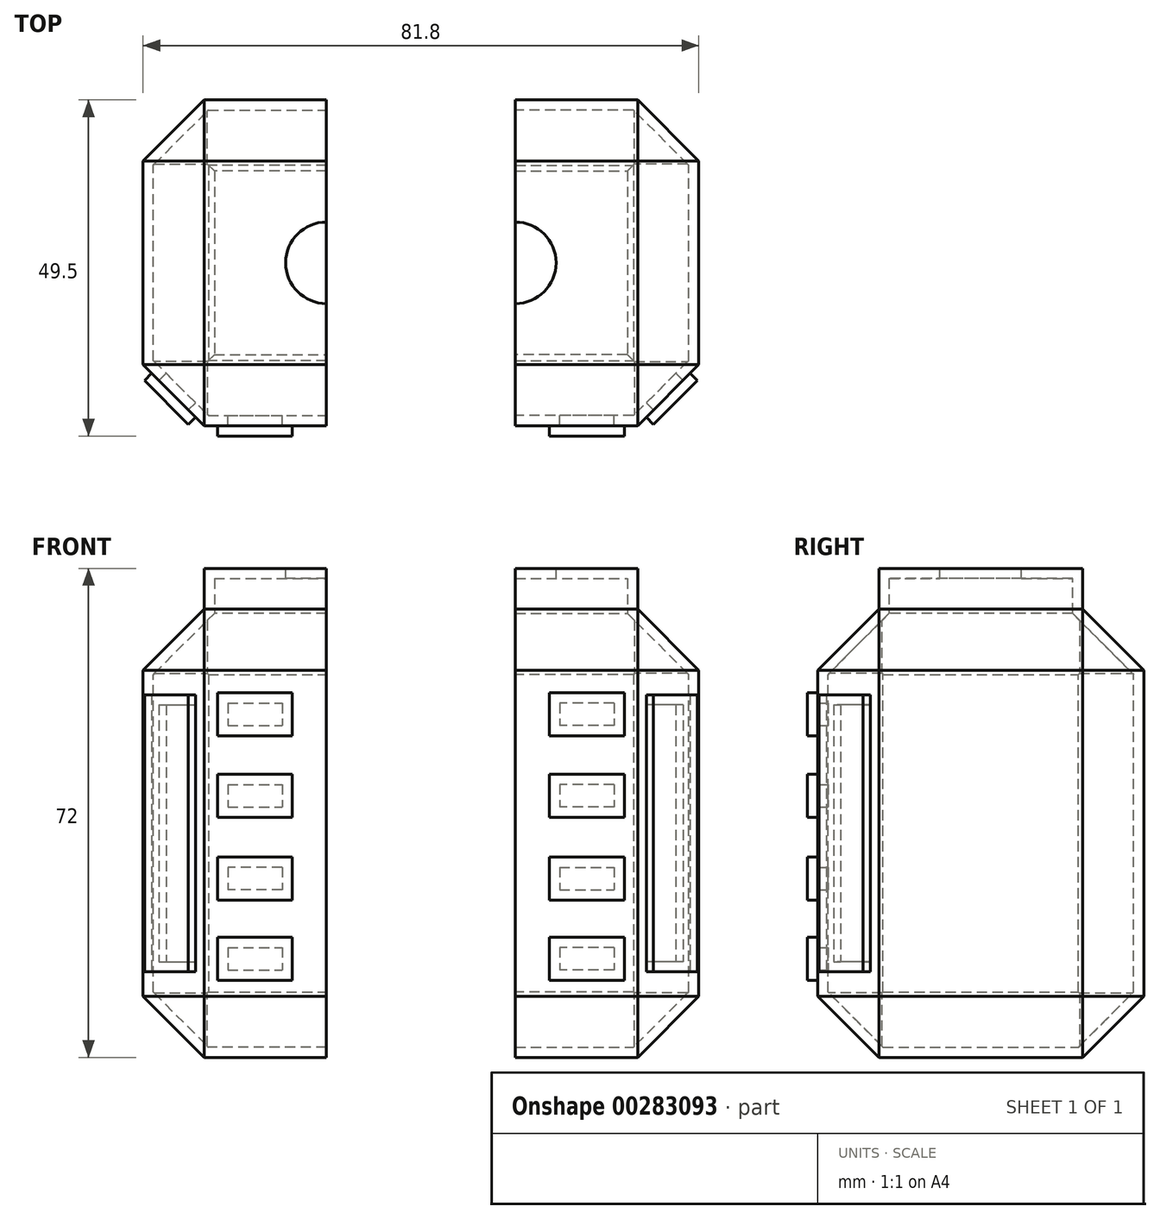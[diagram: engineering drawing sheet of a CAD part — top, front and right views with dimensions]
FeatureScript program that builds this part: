
annotation { "Feature Type Name" : "Feature", "Feature Type Description" : "" }
export const myFeature = defineFeature(function(context is Context, id is Id, definition is map)
    precondition{}
    {
        {
            var Q0;
            Q0=qCreatedBy(makeId("Front.planeOp"),FACE);
            var sketch = newSketch(context, id + "F0", { "sketchPlane" : qUnion([Q0])});
            skLineSegment(sketch, "E0.bottom", {"start": v(-51.64, 31.09) * mm, "end": v(38.36, 31.09) * mm});
            skLineSegment(sketch, "E0.top", {"start": v(-51.64, -78.91) * mm, "end": v(38.36, -78.91) * mm});
            skLineSegment(sketch, "E0.left", {"start": v(-51.64, 31.09) * mm, "end": v(-51.64, -78.91) * mm});
            skLineSegment(sketch, "E0.right", {"start": v(38.36, 31.09) * mm, "end": v(38.36, -78.91) * mm});
            skPoint(sketch, "E1.0", {"position": v(0, 0) * mm});
            skSolve(sketch);
        }
        {
            var Q0;
            Q0=makeQuery(id+"F0.imprint","IMPRINT",FACE,{"disambiguationData":[TD([[makeQuery(id+"F0.imprint","IMPRINT",EDGE,{"derivedFrom":sQuery(id+"F0.wireOp",EDGE,"E0.bottom")}),-1.0]])]});
            extrude(context, id + "F1", {"entities" : qUnion([Q0]), "depth" : 80 * mm});
        }
        {
            var Q0;
            Q0=makeQuery(id+"F1.opExtrude","CAP_EDGE",EDGE,{"disambiguationData":[OSD([sQuery(id+"F0.wireOp",EDGE,"E0.left")])],"isStart":true});
            var Q1;
            Q1=makeQuery(id+"F1.opExtrude","SWEPT_EDGE",EDGE,{"disambiguationData":[OSD([sQuery(id+"F0.wireOp",EDGE,"E0.bottom"),sQuery(id+"F0.wireOp",EDGE,"E0.left")])]});
            var Q2;
            Q2=makeQuery(id+"F1.opExtrude","CAP_EDGE",EDGE,{"disambiguationData":[OSD([sQuery(id+"F0.wireOp",EDGE,"E0.bottom")])],"isStart":true});
            var Q3;
            Q3=makeQuery(id+"F1.opExtrude","CAP_EDGE",EDGE,{"disambiguationData":[OSD([sQuery(id+"F0.wireOp",EDGE,"E0.right")])],"isStart":true});
            var Q4;
            Q4=makeQuery(id+"F1.opExtrude","SWEPT_EDGE",EDGE,{"disambiguationData":[OSD([sQuery(id+"F0.wireOp",EDGE,"E0.top"),sQuery(id+"F0.wireOp",EDGE,"E0.left")])]});
            var Q5;
            Q5=makeQuery(id+"F1.opExtrude","CAP_EDGE",EDGE,{"disambiguationData":[OSD([sQuery(id+"F0.wireOp",EDGE,"E0.top")])],"isStart":true});
            var Q6;
            Q6=makeQuery(id+"F1.opExtrude","CAP_EDGE",EDGE,{"disambiguationData":[OSD([sQuery(id+"F0.wireOp",EDGE,"E0.left")])],"isStart":false});
            var Q7;
            Q7=makeQuery(id+"F1.opExtrude","CAP_EDGE",EDGE,{"disambiguationData":[OSD([sQuery(id+"F0.wireOp",EDGE,"E0.top")])],"isStart":false});
            var Q8;
            Q8=makeQuery(id+"F1.opExtrude","CAP_EDGE",EDGE,{"disambiguationData":[OSD([sQuery(id+"F0.wireOp",EDGE,"E0.right")])],"isStart":false});
            var Q9;
            Q9=makeQuery(id+"F1.opExtrude","CAP_EDGE",EDGE,{"disambiguationData":[OSD([sQuery(id+"F0.wireOp",EDGE,"E0.bottom")])],"isStart":false});
            var Q10;
            Q10=makeQuery(id+"F1.opExtrude","SWEPT_EDGE",EDGE,{"disambiguationData":[OSD([sQuery(id+"F0.wireOp",EDGE,"E0.bottom"),sQuery(id+"F0.wireOp",EDGE,"E0.right")])]});
            var Q11;
            Q11=makeQuery(id+"F1.opExtrude","SWEPT_EDGE",EDGE,{"disambiguationData":[OSD([sQuery(id+"F0.wireOp",EDGE,"E0.top"),sQuery(id+"F0.wireOp",EDGE,"E0.right")])]});
            chamfer(context, id + "F2", {"entities" : qUnion([Q0, Q1, Q2, Q3, Q4, Q5, Q6, Q7, Q8, Q9, Q10, Q11]), "width" : 15 * mm, "tangentPropagation" : true});
        }
        {
            var Q0;
            Q0=makeQuery(id+"F1.opExtrude","SWEPT_FACE",FACE,{"disambiguationData":[OSD([sQuery(id+"F0.wireOp",EDGE,"E0.bottom")])]});
            extrude(context, id + "F3", {"entities" : qUnion([Q0]), "operationType" : NewBodyOperationType.ADD, "depth" : 10 * mm});
        }
        {
            var Q0;
            {var subQ0=sQuery(id+"F0.wireOp",EDGE,"E0.bottom");Q0=makeQuery(id+"F3.opExtrude","SWEPT_FACE",FACE,{"disambiguationData":[OSD([subQ0]),TDD([makeQuery(id+"F2.opChamfer","BLEND_EDGE",EDGE,{"blendedFrom":[makeQuery(id+"F1.opExtrude","CAP_EDGE",EDGE,{"disambiguationData":[OSD([subQ0])],"isStart":false}),makeQuery(id+"F1.opExtrude","SWEPT_FACE",FACE,{"disambiguationData":[OSD([subQ0])]})],"blendedInto":[makeQuery(id+"F1.opExtrude","SWEPT_FACE",FACE,{"disambiguationData":[OSD([subQ0])]})]})])]});}
            cPlane(context, id + "F4", {"entities" : qUnion([Q0]), "cplaneType" : CPlaneType.OFFSET, "offset" : 9.9 * mm, "oppositeDirection" : true, "width" : 150 * mm, "height" : 150 * mm});
        }
        {
            var Q0;
            Q0=makeQuery(id+"F1.opExtrude","CAP_FACE",FACE,{"disambiguationData":[OSD([sQuery(id+"F0.wireOp",EDGE,"E0.bottom"),sQuery(id+"F0.wireOp",EDGE,"E0.top"),sQuery(id+"F0.wireOp",EDGE,"E0.left"),sQuery(id+"F0.wireOp",EDGE,"E0.right")])],"isStart":false});
            var sketch = newSketch(context, id + "F5", { "sketchPlane" : qUnion([Q0])});
            skLineSegment(sketch, "E2.bottom", {"start": v(-33.35, 10.54) * mm, "end": v(-15, 10.54) * mm});
            skLineSegment(sketch, "E2.top", {"start": v(-33.35, 0) * mm, "end": v(-15, 0) * mm});
            skLineSegment(sketch, "E2.left", {"start": v(-33.35, 10.54) * mm, "end": v(-33.35, 0) * mm});
            skLineSegment(sketch, "E2.right", {"start": v(-15, 10.54) * mm, "end": v(-15, 0) * mm});
            skLineSegment(sketch, "E3.bottom", {"start": v(0, 10.54) * mm, "end": v(19.36, 10.54) * mm});
            skLineSegment(sketch, "E3.top", {"start": v(0, 0) * mm, "end": v(19.36, 0) * mm});
            skLineSegment(sketch, "E3.left", {"start": v(0, 10.54) * mm, "end": v(0, 0) * mm});
            skLineSegment(sketch, "E3.right", {"start": v(19.36, 10.54) * mm, "end": v(19.36, 0) * mm});
            skLineSegment(sketch, "E4.bottom", {"start": v(-33.35, -9.45) * mm, "end": v(-15, -9.45) * mm});
            skLineSegment(sketch, "E4.top", {"start": v(-33.35, -20) * mm, "end": v(-15, -20) * mm});
            skLineSegment(sketch, "E4.left", {"start": v(-33.35, -9.45) * mm, "end": v(-33.35, -20) * mm});
            skLineSegment(sketch, "E4.right", {"start": v(-15, -9.45) * mm, "end": v(-15, -20) * mm});
            skLineSegment(sketch, "E5.bottom", {"start": v(0, -9.45) * mm, "end": v(19.36, -9.45) * mm});
            skLineSegment(sketch, "E5.top", {"start": v(0, -20) * mm, "end": v(19.36, -20) * mm});
            skLineSegment(sketch, "E5.left", {"start": v(0, -9.45) * mm, "end": v(0, -20) * mm});
            skLineSegment(sketch, "E5.right", {"start": v(19.36, -9.45) * mm, "end": v(19.36, -20) * mm});
            skLineSegment(sketch, "E6.bottom", {"start": v(-15, -29.77) * mm, "end": v(-33.35, -29.77) * mm});
            skLineSegment(sketch, "E6.top", {"start": v(-15, -40.3) * mm, "end": v(-33.35, -40.3) * mm});
            skLineSegment(sketch, "E6.left", {"start": v(-15, -29.77) * mm, "end": v(-15, -40.3) * mm});
            skLineSegment(sketch, "E6.right", {"start": v(-33.35, -29.77) * mm, "end": v(-33.35, -40.3) * mm});
            skLineSegment(sketch, "E7.bottom", {"start": v(0, -29.77) * mm, "end": v(19.36, -29.77) * mm});
            skLineSegment(sketch, "E7.top", {"start": v(0, -40.3) * mm, "end": v(19.36, -40.3) * mm});
            skLineSegment(sketch, "E7.left", {"start": v(0, -29.77) * mm, "end": v(0, -40.3) * mm});
            skLineSegment(sketch, "E7.right", {"start": v(19.36, -29.77) * mm, "end": v(19.36, -40.3) * mm});
            skLineSegment(sketch, "E8.bottom", {"start": v(-33.35, -49.43) * mm, "end": v(-15, -49.43) * mm});
            skLineSegment(sketch, "E8.top", {"start": v(-33.35, -59.97) * mm, "end": v(-15, -59.97) * mm});
            skLineSegment(sketch, "E8.left", {"start": v(-33.35, -49.43) * mm, "end": v(-33.35, -59.97) * mm});
            skLineSegment(sketch, "E8.right", {"start": v(-15, -49.43) * mm, "end": v(-15, -59.97) * mm});
            skLineSegment(sketch, "E9.bottom", {"start": v(0, -49.43) * mm, "end": v(19.36, -49.43) * mm});
            skLineSegment(sketch, "E9.top", {"start": v(0, -59.97) * mm, "end": v(19.36, -59.97) * mm});
            skLineSegment(sketch, "E9.left", {"start": v(0, -49.43) * mm, "end": v(0, -59.97) * mm});
            skLineSegment(sketch, "E9.right", {"start": v(19.36, -49.43) * mm, "end": v(19.36, -59.97) * mm});
            skSolve(sketch);
        }
        {
            var Q0;
            Q0=qSketchRegion(id+"F5",true);
            extrude(context, id + "F6", {"entities" : qUnion([Q0]), "operationType" : NewBodyOperationType.ADD, "depth" : 2.5 * mm});
        }
        {
            var Q0;
            {var subQ0=sQuery(id+"F0.wireOp",EDGE,"E0.right");Q0=makeQuery(id+"F2.opChamfer","BLEND_FACE",FACE,{"disambiguationData":[OSD([subQ0]),TDD([makeQuery(id+"F1.opExtrude","CAP_EDGE",EDGE,{"disambiguationData":[OSD([subQ0])],"isStart":false})])]});}
            var sketch = newSketch(context, id + "F7", { "sketchPlane" : qUnion([Q0])});
            skLineSegment(sketch, "E10.bottom", {"start": v(-37.05, 10.09) * mm, "end": v(-21.83, 10.09) * mm});
            skLineSegment(sketch, "E10.top", {"start": v(-37.05, -57.91) * mm, "end": v(-21.83, -57.91) * mm});
            skLineSegment(sketch, "E10.left", {"start": v(-37.05, 10.09) * mm, "end": v(-37.05, -57.91) * mm});
            skLineSegment(sketch, "E10.right", {"start": v(-21.83, 10.09) * mm, "end": v(-21.83, -57.91) * mm});
            skSolve(sketch);
        }
        {
            var Q0;
            Q0=makeQuery(id+"F7.imprint","IMPRINT",FACE,{"disambiguationData":[TD([[makeQuery(id+"F7.imprint","IMPRINT",EDGE,{"derivedFrom":sQuery(id+"F7.wireOp",EDGE,"E10.bottom")}),-1.0]])]});
            extrude(context, id + "F8", {"entities" : qUnion([Q0]), "operationType" : NewBodyOperationType.ADD, "depth" : 2.5 * mm});
        }
        {
            var Q0;
            {var subQ0=sQuery(id+"F0.wireOp",EDGE,"E0.left");Q0=makeQuery(id+"F2.opChamfer","BLEND_FACE",FACE,{"disambiguationData":[OSD([subQ0]),TDD([makeQuery(id+"F1.opExtrude","CAP_EDGE",EDGE,{"disambiguationData":[OSD([subQ0])],"isStart":false})])]});}
            var sketch = newSketch(context, id + "F9", { "sketchPlane" : qUnion([Q0])});
            skLineSegment(sketch, "E11.bottom", {"start": v(12.45, 10.09) * mm, "end": v(27.66, 10.09) * mm});
            skLineSegment(sketch, "E11.top", {"start": v(12.45, -57.91) * mm, "end": v(27.66, -57.91) * mm});
            skLineSegment(sketch, "E11.left", {"start": v(12.45, 10.09) * mm, "end": v(12.45, -57.91) * mm});
            skLineSegment(sketch, "E11.right", {"start": v(27.66, 10.09) * mm, "end": v(27.66, -57.91) * mm});
            skSolve(sketch);
        }
        {
            var Q0;
            Q0=makeQuery(id+"F9.imprint","IMPRINT",FACE,{"disambiguationData":[TD([[makeQuery(id+"F9.imprint","IMPRINT",EDGE,{"derivedFrom":sQuery(id+"F9.wireOp",EDGE,"E11.bottom")}),-1.0]])]});
            extrude(context, id + "F10", {"entities" : qUnion([Q0]), "operationType" : NewBodyOperationType.ADD, "depth" : 2.5 * mm});
        }
        {
            var Q0;
            Q0=makeQuery(id+"F3.opExtrude","CAP_FACE",FACE,{"disambiguationData":[OSD([sQuery(id+"F0.wireOp",EDGE,"E0.bottom")])],"isStart":false});
            var sketch = newSketch(context, id + "F11", { "sketchPlane" : qUnion([Q0])});
            skLineSegment(sketch, "E12", {"start": v(-6.64, -15) * mm, "end": v(-6.64, 15.48) * mm});
            skLineSegment(sketch, "E13", {"start": v(-6.64, 15.48) * mm, "end": v(68.24, 15.48) * mm});
            skLineSegment(sketch, "E14", {"start": v(68.24, 15.48) * mm, "end": v(68.24, -91.44) * mm});
            skLineSegment(sketch, "E15", {"start": v(68.24, -91.44) * mm, "end": v(-6.64, -91.44) * mm});
            skPoint(sketch, "E15.endSnap0", {"position": v(-6.64, -65) * mm});
            skLineSegment(sketch, "E16", {"start": v(-6.64, -15) * mm, "end": v(-6.64, -91.44) * mm});
            skSolve(sketch);
        }
        {
            var Q0;
            Q0 = qSketchRegion(id + "F11", true);
            extrude(context, id + "F12", {"entities" : qUnion([Q0]), "operationType" : NewBodyOperationType.REMOVE, "oppositeDirection" : true, "depth" : 157.1 * mm});
        }
        {
            var Q0;
            Q0=makeQuery(id+"F12.boolean.opBoolean","COPY",FACE,{"derivedFrom":makeQuery(id+"F12.opExtrude","SWEPT_FACE",FACE,{"disambiguationData":[OSD([sQuery(id+"F11.wireOp",EDGE,"E12"),sQuery(id+"F11.wireOp",EDGE,"E16")])]})});
            shell(context, id + "F13", {"entities" : qUnion([Q0]), "thickness" : 2.5 * mm});
        }
        {
            var Q0;
            Q0=makeQuery(id+"F3.opExtrude","CAP_FACE",FACE,{"disambiguationData":[OSD([sQuery(id+"F0.wireOp",EDGE,"E0.bottom")])],"isStart":false});
            var sketch = newSketch(context, id + "F14", { "sketchPlane" : qUnion([Q0])});
            skSolve(sketch);
        }
        {
            var Q0;
            {var subQ0=sQuery(id+"F0.wireOp",EDGE,"E0.bottom");var subQ1=makeQuery(id+"F1.opExtrude","SWEPT_FACE",FACE,{"disambiguationData":[OSD([subQ0])]});Q0=makeQuery(id+"F14.imprint","IMPRINT",FACE,{"disambiguationData":[TD([[makeQuery(id+"F14.imprint","IMPRINT",EDGE,{"derivedFrom":makeQuery(id+"F3.opExtrude","CAP_EDGE",EDGE,{"disambiguationData":[OSD([subQ0]),TDD([makeQuery(id+"F2.opChamfer","BLEND_EDGE",EDGE,{"blendedFrom":[makeQuery(id+"F1.opExtrude","CAP_EDGE",EDGE,{"disambiguationData":[OSD([subQ0])],"isStart":true}),subQ1],"blendedInto":[subQ1]})])],"isStart":false})}),1.0]])]});}
            var sketch = newSketch(context, id + "F15", { "sketchPlane" : qUnion([Q0])});
            skPoint(sketch, "E17.0", {"position": v(-6.64, -40) * mm});
            skCircle(sketch, "E18", {"center": v(-6.64, -40) * mm, "radius": 10 * mm});
            skSolve(sketch);
        }
        {
            var Q0;
            Q0 = qSketchRegion(id + "F15", true);
            extrude(context, id + "F16", {"entities" : qUnion([Q0]), "operationType" : NewBodyOperationType.REMOVE, "oppositeDirection" : true, "depth" : 25 * mm});
        }
        {
            var Q0;
            Q0=makeQuery(id+"F1.opExtrude","SWEPT_BODY",BODY,{"disambiguationData":[OSD([sQuery(id+"F0.wireOp",EDGE,"E0.bottom"),sQuery(id+"F0.wireOp",EDGE,"E0.top"),sQuery(id+"F0.wireOp",EDGE,"E0.left"),sQuery(id+"F0.wireOp",EDGE,"E0.right")])]});
            var Q1;
            Q1=qCreatedBy(makeId("Origin.pointOp"),VERTEX);
            transform(context, id + "F17", {"entities" : qUnion([Q0]), "transformType" : TransformType.SCALE_UNIFORMLY, "scale" : .6, "scalePoint" : qUnion([Q1]), "makeCopy" : false});
        }
        {
            var Q0;
            Q0=makeQuery(id+"F1.opExtrude","SWEPT_BODY",BODY,{"disambiguationData":[OSD([sQuery(id+"F0.wireOp",EDGE,"E0.bottom"),sQuery(id+"F0.wireOp",EDGE,"E0.top"),sQuery(id+"F0.wireOp",EDGE,"E0.left"),sQuery(id+"F0.wireOp",EDGE,"E0.right")])]});
            var Q1;
            Q1=makeQuery(id+"F12.boolean.opBoolean","COPY",FACE,{"derivedFrom":makeQuery(id+"F12.opExtrude","SWEPT_FACE",FACE,{"disambiguationData":[OSD([sQuery(id+"F11.wireOp",EDGE,"E12"),sQuery(id+"F11.wireOp",EDGE,"E16")])]})});
            mirror(context, id + "F18", {"entities" : qUnion([Q0]), "mirrorPlane" : qUnion([Q1])});
        }
        {
            var Q0;
            Q0=makeQuery(id+"F18.opPattern","COPY",BODY,{"derivedFrom":makeQuery(id+"F1.opExtrude","SWEPT_BODY",BODY,{"disambiguationData":[OSD([sQuery(id+"F0.wireOp",EDGE,"E0.bottom"),sQuery(id+"F0.wireOp",EDGE,"E0.top"),sQuery(id+"F0.wireOp",EDGE,"E0.left"),sQuery(id+"F0.wireOp",EDGE,"E0.right")])]}),"instanceName":"1"});
            transform(context, id + "F19", {"entities" : qUnion([Q0]), "transformType" : TransformType.TRANSLATION_3D, "dx" : 27.8 * mm, "dy" : 0 * mm, "dz" : 0 * mm, "makeCopy" : false});
        }
    });
